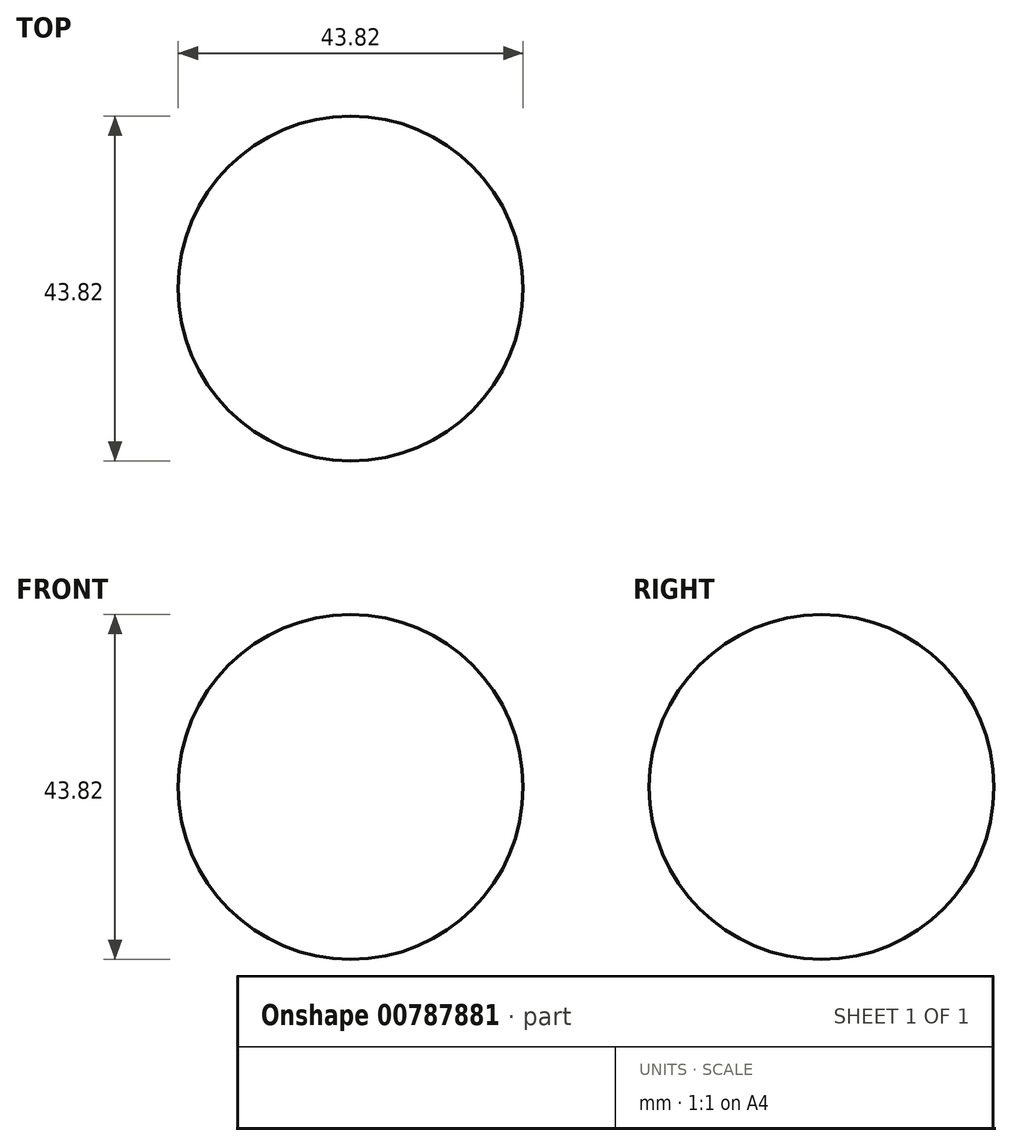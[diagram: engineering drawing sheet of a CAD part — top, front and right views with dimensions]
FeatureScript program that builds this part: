
annotation { "Feature Type Name" : "Feature", "Feature Type Description" : "" }
export const myFeature = defineFeature(function(context is Context, id is Id, definition is map)
    precondition{}
    {
        {
            var Q0;
            Q0=qCreatedBy(makeId("Front.planeOp"),FACE);
            var sketch = newSketch(context, id + "F0", { "sketchPlane" : qUnion([Q0])});
            skCircle(sketch, "E0", {"center": v(0, 0) * mm, "radius": 21.9 * mm});
            skLineSegment(sketch, "E1", {"start": v(-37.47, 0) * mm, "end": v(47.69, 0) * mm});
            skSolve(sketch);
        }
        {
            var Q0;
            {var subQ0=sQuery(id+"F0.wireOp",EDGE,"E1");var subQ1=sQuery(id+"F0.wireOp",EDGE,"E0");var subQ2=makeQuery(id+"F0.imprint","INTERSECT",VERTEX,{"disambiguationData":[OD(0.0)],"derivedFrom":[subQ1,subQ0]});Q0=makeQuery(id+"F0.imprint","IMPRINT",FACE,{"disambiguationData":[TD([[makeQuery(id+"F0.imprint","IMPRINT",EDGE,{"disambiguationData":[TD([[subQ2,-1.0]])],"derivedFrom":subQ1}),1.0]])]});}
            var Q1;
            Q1=sQuery(id+"F0.wireOp",EDGE,"E1");
            revolve(context, id + "F1", {"surfaceOperationType" : NewSurfaceOperationType.NEW, "entities" : qUnion([Q0]), "axis" : qUnion([Q1]), "revolveType" : RevolveType.FULL});
        }
    });
